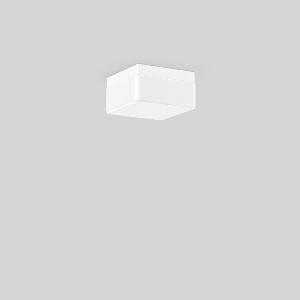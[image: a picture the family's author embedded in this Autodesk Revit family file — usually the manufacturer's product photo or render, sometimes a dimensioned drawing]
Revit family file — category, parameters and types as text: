
# Revit family: quadrat_21127_002_aa75
name_source: partatom
category: Lighting Fixtures
units: mm (PartAtom-declared; Revit-internal decimal feet)

## family parameters
Cut with Voids When Loaded = No
Host = Face
Light Source = No
Part Type = Normal
Room Calculation Point = No
Round Connector Dimension = Use Diameter
Shared = No

## types (1)
- QUADRAT (1 x QA60/clear E27, 700 lm, 46 W, 3000)
    Apparent Load = 46 VA
    CIE Flux Codes = 35 64 86 74 50
    Color Rendering = 90
    Color Temperature = 3000
    Default Elevation = 1800 mm
    Description = Series: QUADRAT
Square surface-mounted luminaire in classic design. Base: plastic. Opal glass: mouth-blown, satin finish. Diffuser fastening: spring system. Suitable for Ceiling mounting, Wall (surface). IP 43 ceiling mounting, IP 44 wall mounting. 
Colour: white
Length: 190 mm
Width: 190 mm
Height: 100 mm
Lamp: A60
Number of lamps: 1
Wattage: 60 W
Socket: E27
System power: 46 W
Rated luminous flux: 350 lm
Luminous efficiency: 8 lm/W
Control gear: Converter not necessary
Protection class: II
Type of protection: IP 43
    Height = 100 mm  [stored 0.328084 ft]
    Lamp = 1 x QA60/clear E27
    Lamp Light Flux = 700 lm
    Lamp Power = 46 W
    Lamp count = 1
    Length = 190 mm  [stored 0.62336 ft]
    Lifetime = 3000 h
    Luminous efficacy = 8 lm/W
    Manufacturer = RZB
    ModVariant = No
    Model = 21127.002
    Mounting Place = Ceiling, Wall
    Mounting Type = Surface mounted
    Number of Poles = 1
    OnlyDefault = Yes
    Power Factor = 1
    Product Name = QUADRAT
    Product group = Surface mounted ceiling and wall luminaires
    ProductGroupID = 305
    Protection Class = Protection class II
    Protection Degree = IP 43
    RLX_Detail_Level = 1
    RLX_Emergency_Light_Flux = 0 lm
    RLX_Emergency_Type = 0
    RLX_Emergency_Type_DB = No
    RlxData = <blob elided: 8949 chars, md5=e741190c>
    Socket = E27
    Standby Power = 0 W
    System Light Flux = 352 lm
    System Power = 46 W
    Type Comments = Product without accessories
    Type Image = 21127.002.jpg
    URL = http://relux.com
    VarID = ---
    Voltage = 230 V
    Voltage Range = 220-240 V
    Weight = 0.00 kg
    Width = 190 mm  [stored 0.62336 ft]

note: [stored X ft] marks values corroborated as IEEE doubles in the binary element streams (Revit-internal decimal feet)

## geometry (parser evidence)
native form markers: Sweep x10
no freeform markers — native parametric forms only
